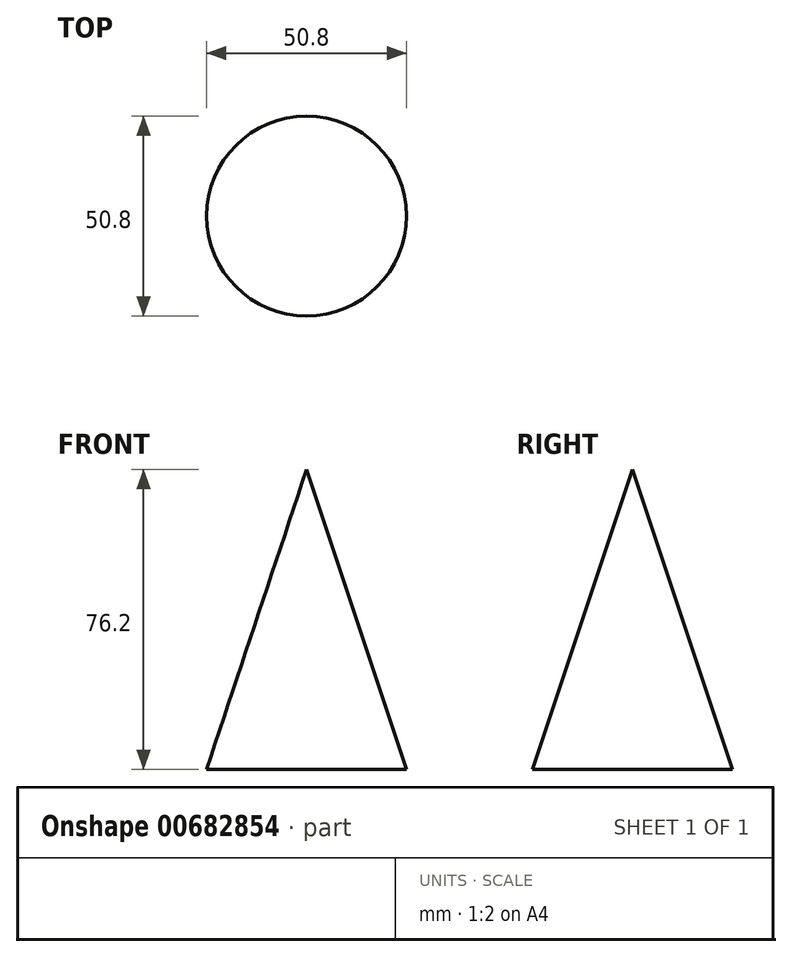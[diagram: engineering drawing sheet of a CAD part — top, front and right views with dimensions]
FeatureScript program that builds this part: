
annotation { "Feature Type Name" : "Feature", "Feature Type Description" : "" }
export const myFeature = defineFeature(function(context is Context, id is Id, definition is map)
    precondition{}
    {
        {
            var Q0;
            Q0=qCreatedBy(makeId("Front.planeOp"),FACE);
            var sketch = newSketch(context, id + "F0", { "sketchPlane" : qUnion([Q0])});
            skLineSegment(sketch, "E0", {"start": v(0, 0) * mm, "end": v(-25.4, 0) * mm});
            skLineSegment(sketch, "E1", {"start": v(-25.4, 0) * mm, "end": v(0, 76.2) * mm});
            skLineSegment(sketch, "E2", {"start": v(0, 76.2) * mm, "end": v(0, 0) * mm});
            skSolve(sketch);
        }
        {
            var Q0;
            Q0=makeQuery(id+"F0.imprint","IMPRINT",FACE,{"disambiguationData":[TD([[makeQuery(id+"F0.imprint","IMPRINT",EDGE,{"derivedFrom":sQuery(id+"F0.wireOp",EDGE,"E0")}),-1.0]])]});
            var Q1;
            Q1=sQuery(id+"F0.wireOp",EDGE,"E2");
            revolve(context, id + "F1", {"entities" : qUnion([Q0]), "axis" : qUnion([Q1]), "revolveType" : RevolveType.FULL});
        }
    });
